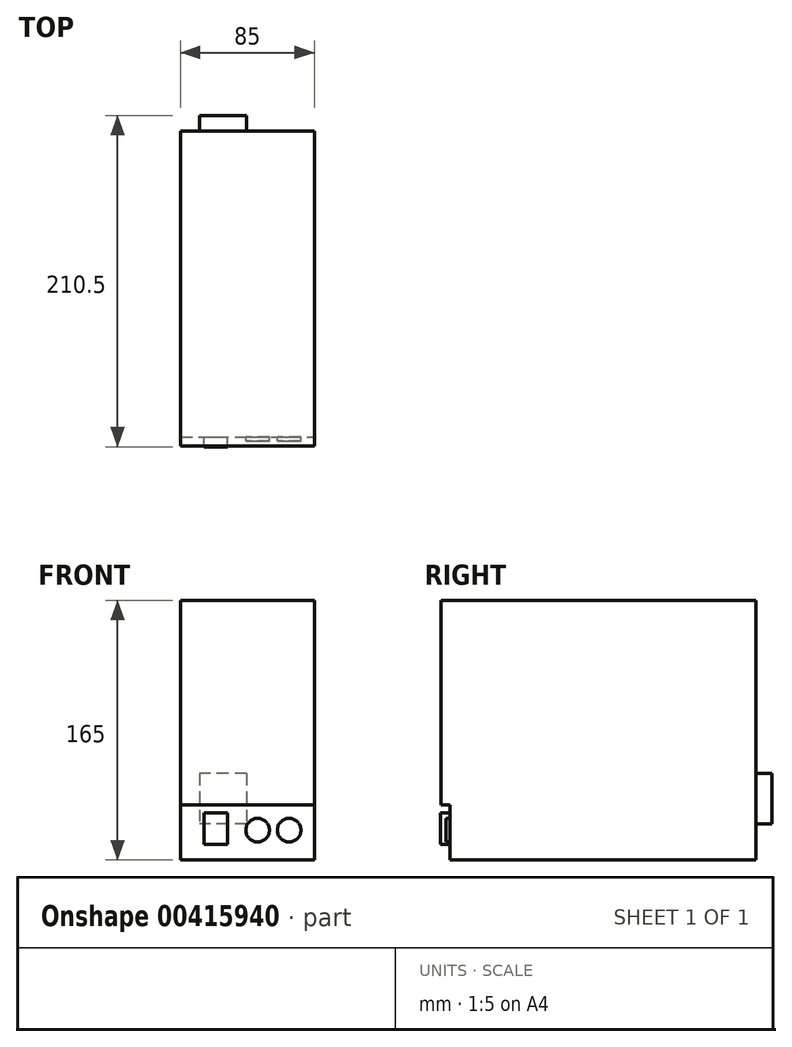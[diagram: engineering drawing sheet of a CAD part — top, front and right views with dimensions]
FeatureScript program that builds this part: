
annotation { "Feature Type Name" : "Feature", "Feature Type Description" : "" }
export const myFeature = defineFeature(function(context is Context, id is Id, definition is map)
    precondition{}
    {
        {
            var Q0;
            Q0=qCreatedBy(makeId("Front.planeOp"),FACE);
            var sketch = newSketch(context, id + "F0", { "sketchPlane" : qUnion([Q0])});
            skLineSegment(sketch, "E0.bottom", {"start": v(-42.5, 82.5) * mm, "end": v(42.5, 82.5) * mm});
            skLineSegment(sketch, "E0.top", {"start": v(-42.5, -82.5) * mm, "end": v(42.5, -82.5) * mm});
            skLineSegment(sketch, "E0.left", {"start": v(-42.5, 82.5) * mm, "end": v(-42.5, -82.5) * mm});
            skLineSegment(sketch, "E0.right", {"start": v(42.5, 82.5) * mm, "end": v(42.5, -82.5) * mm});
            skPoint(sketch, "E0.middle", {"position": v(0, 0) * mm});
            skSolve(sketch);
        }
        {
            var Q0;
            Q0=makeQuery(id+"F0.imprint","IMPRINT",FACE,{"disambiguationData":[TD([[makeQuery(id+"F0.imprint","IMPRINT",EDGE,{"derivedFrom":sQuery(id+"F0.wireOp",EDGE,"E0.bottom")}),-1.0]])]});
            extrude(context, id + "F1", {"entities" : qUnion([Q0]), "endBound" : BoundingType.SYMMETRIC, "depth" : 200 * mm});
        }
        {
            var Q0;
            Q0=makeQuery(id+"F1.opExtrude","CAP_FACE",FACE,{"disambiguationData":[OSD([sQuery(id+"F0.wireOp",EDGE,"E0.bottom"),sQuery(id+"F0.wireOp",EDGE,"E0.top"),sQuery(id+"F0.wireOp",EDGE,"E0.left"),sQuery(id+"F0.wireOp",EDGE,"E0.right")])],"isStart":true});
            var sketch = newSketch(context, id + "F2", { "sketchPlane" : qUnion([Q0])});
            skLineSegment(sketch, "E1.bottom", {"start": v(0.5, -27.5) * mm, "end": v(30.5, -27.5) * mm});
            skLineSegment(sketch, "E1.top", {"start": v(0.5, -59.5) * mm, "end": v(30.5, -59.5) * mm});
            skLineSegment(sketch, "E1.left", {"start": v(0.5, -27.5) * mm, "end": v(0.5, -59.5) * mm});
            skLineSegment(sketch, "E1.right", {"start": v(30.5, -27.5) * mm, "end": v(30.5, -59.5) * mm});
            skSolve(sketch);
        }
        {
            var Q0;
            Q0=makeQuery(id+"F2.imprint","IMPRINT",FACE,{"disambiguationData":[TD([[makeQuery(id+"F2.imprint","IMPRINT",EDGE,{"derivedFrom":sQuery(id+"F2.wireOp",EDGE,"E1.bottom")}),-1.0]])]});
            extrude(context, id + "F3", {"entities" : qUnion([Q0]), "operationType" : NewBodyOperationType.ADD, "depth" : 10 * mm});
        }
        {
            var Q0;
            Q0=makeQuery(id+"F1.opExtrude","CAP_FACE",FACE,{"disambiguationData":[OSD([sQuery(id+"F0.wireOp",EDGE,"E0.bottom"),sQuery(id+"F0.wireOp",EDGE,"E0.top"),sQuery(id+"F0.wireOp",EDGE,"E0.left"),sQuery(id+"F0.wireOp",EDGE,"E0.right")])],"isStart":false});
            var sketch = newSketch(context, id + "F4", { "sketchPlane" : qUnion([Q0])});
            skLineSegment(sketch, "E2.bottom", {"start": v(-42.5, 82.5) * mm, "end": v(42.5, 82.5) * mm});
            skLineSegment(sketch, "E2.top", {"start": v(-42.5, -47.5) * mm, "end": v(42.5, -47.5) * mm});
            skLineSegment(sketch, "E2.left", {"start": v(-42.5, 82.5) * mm, "end": v(-42.5, -47.5) * mm});
            skLineSegment(sketch, "E2.right", {"start": v(42.5, 82.5) * mm, "end": v(42.5, -47.5) * mm});
            skSolve(sketch);
        }
        {
            var Q0;
            {var subQ0=sQuery(id+"F4.wireOp",EDGE,"E2.top");Q0=makeQuery(id+"F4.imprint","IMPRINT",FACE,{"disambiguationData":[TD([[makeQuery(id+"F4.imprint","IMPRINT",EDGE,{"derivedFrom":subQ0}),-1.0]])]});}
            extrude(context, id + "F5", {"entities" : qUnion([Q0]), "operationType" : NewBodyOperationType.REMOVE, "oppositeDirection" : true, "depth" : 5.7 * mm});
        }
        {
            var Q0;
            Q0=makeQuery(id+"F5.boolean.opBoolean","COPY",FACE,{"derivedFrom":makeQuery(id+"F5.opExtrude","CAP_FACE",FACE,{"disambiguationData":[OSD([sQuery(id+"F0.wireOp",EDGE,"E0.top"),sQuery(id+"F0.wireOp",EDGE,"E0.left"),sQuery(id+"F0.wireOp",EDGE,"E0.right"),sQuery(id+"F4.wireOp",EDGE,"E2.top")])],"isStart":false})});
            var sketch = newSketch(context, id + "F6", { "sketchPlane" : qUnion([Q0])});
            skCircle(sketch, "E3", {"center": v(6.5, -63.5) * mm, "radius": 7.5 * mm});
            skCircle(sketch, "E4", {"center": v(26.5, -63.5) * mm, "radius": 7.5 * mm});
            skSolve(sketch);
        }
        {
            var Q0;
            Q0=makeQuery(id+"F6.imprint","IMPRINT",FACE,{"disambiguationData":[TD([[makeQuery(id+"F6.imprint","IMPRINT",EDGE,{"derivedFrom":sQuery(id+"F6.wireOp",EDGE,"E3")}),1.0]])]});
            var Q1;
            Q1=makeQuery(id+"F6.imprint","IMPRINT",FACE,{"disambiguationData":[TD([[makeQuery(id+"F6.imprint","IMPRINT",EDGE,{"derivedFrom":sQuery(id+"F6.wireOp",EDGE,"E4")}),1.0]])]});
            extrude(context, id + "F7", {"entities" : qUnion([Q0, Q1]), "operationType" : NewBodyOperationType.ADD, "depth" : 2.6 * mm});
        }
        {
            var Q0;
            Q0=makeQuery(id+"F5.boolean.opBoolean","COPY",FACE,{"derivedFrom":makeQuery(id+"F5.opExtrude","CAP_FACE",FACE,{"disambiguationData":[OSD([sQuery(id+"F0.wireOp",EDGE,"E0.top"),sQuery(id+"F0.wireOp",EDGE,"E0.left"),sQuery(id+"F0.wireOp",EDGE,"E0.right"),sQuery(id+"F4.wireOp",EDGE,"E2.top")])],"isStart":false})});
            var sketch = newSketch(context, id + "F8", { "sketchPlane" : qUnion([Q0])});
            skLineSegment(sketch, "E5.bottom", {"start": v(-27.5, -52.5) * mm, "end": v(-12.5, -52.5) * mm});
            skLineSegment(sketch, "E5.top", {"start": v(-27.5, -72.5) * mm, "end": v(-12.5, -72.5) * mm});
            skLineSegment(sketch, "E5.left", {"start": v(-27.5, -52.5) * mm, "end": v(-27.5, -72.5) * mm});
            skLineSegment(sketch, "E5.right", {"start": v(-12.5, -52.5) * mm, "end": v(-12.5, -72.5) * mm});
            skSolve(sketch);
        }
        {
            var Q0;
            Q0=makeQuery(id+"F8.imprint","IMPRINT",FACE,{"disambiguationData":[TD([[makeQuery(id+"F8.imprint","IMPRINT",EDGE,{"derivedFrom":sQuery(id+"F8.wireOp",EDGE,"E5.bottom")}),-1.0]])]});
            extrude(context, id + "F9", {"entities" : qUnion([Q0]), "operationType" : NewBodyOperationType.ADD, "depth" : 6.2 * mm});
        }
    });
